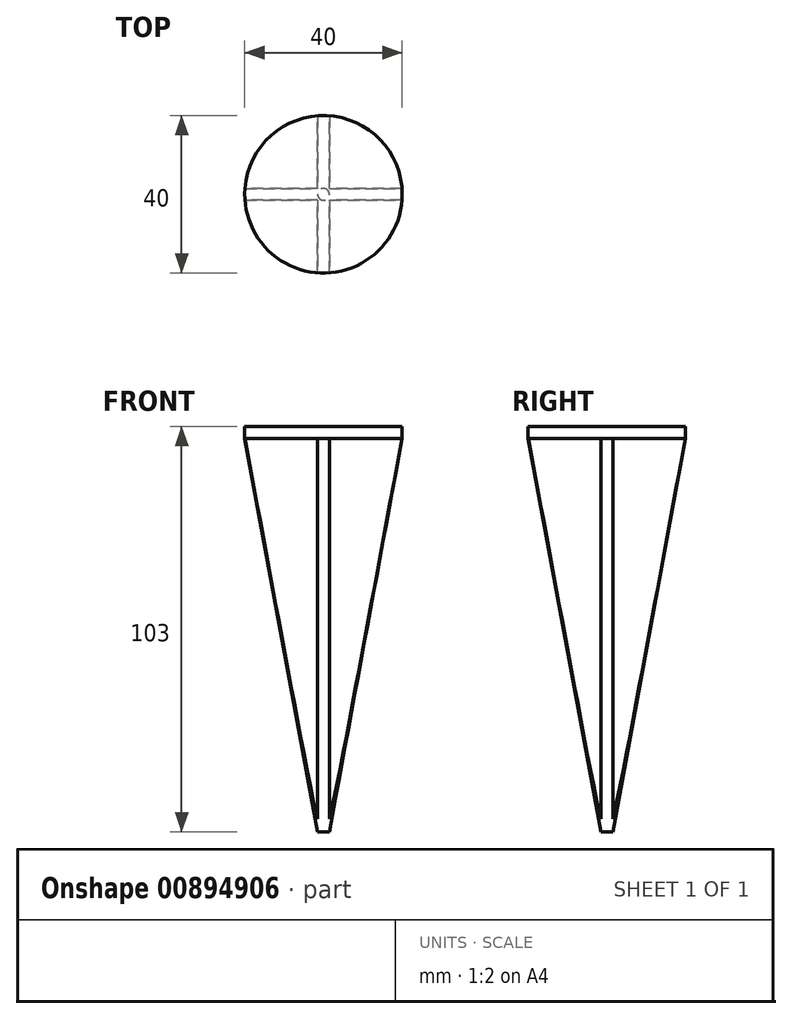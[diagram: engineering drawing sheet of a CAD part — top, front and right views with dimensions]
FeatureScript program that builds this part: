
annotation { "Feature Type Name" : "Feature", "Feature Type Description" : "" }
export const myFeature = defineFeature(function(context is Context, id is Id, definition is map)
    precondition{}
    {
        {
            var Q0;
            Q0=qCreatedBy(makeId("Top.planeOp"),FACE);
            var sketch = newSketch(context, id + "F0", { "sketchPlane" : qUnion([Q0])});
            skCircle(sketch, "E0", {"center": v(0, 0) * mm, "radius": 20 * mm});
            skLineSegment(sketch, "E1.bottom", {"start": v(-19.94, -1.5) * mm, "end": v(-1.5, -1.5) * mm});
            skLineSegment(sketch, "E1.top", {"start": v(-19.94, 1.5) * mm, "end": v(-1.5, 1.5) * mm});
            skLineSegment(sketch, "E2.left", {"start": v(1.5, -19.94) * mm, "end": v(1.5, -1.5) * mm});
            skLineSegment(sketch, "E2.right", {"start": v(-1.5, -19.94) * mm, "end": v(-1.5, -1.5) * mm});
            skLineSegment(sketch, "E3.trimOffspring", {"start": v(-1.5, 1.5) * mm, "end": v(-1.5, 19.94) * mm});
            skLineSegment(sketch, "E4.trimOffspring", {"start": v(1.5, 1.5) * mm, "end": v(19.94, 1.5) * mm});
            skLineSegment(sketch, "E5.trimOffspring", {"start": v(1.5, 1.5) * mm, "end": v(1.5, 19.94) * mm});
            skLineSegment(sketch, "E6.trimOffspring", {"start": v(1.5, -1.5) * mm, "end": v(19.94, -1.5) * mm});
            skSolve(sketch);
        }
        {
            var Q0;
            {var subQ0=sQuery(id+"F0.wireOp",EDGE,"E1.top");Q0=makeQuery(id+"F0.imprint","IMPRINT",FACE,{"disambiguationData":[TD([[makeQuery(id+"F0.imprint","IMPRINT",EDGE,{"derivedFrom":subQ0}),1.0]])]});}
            var Q1;
            {var subQ4=sQuery(id+"F0.wireOp",EDGE,"E1.bottom");Q1=makeQuery(id+"F0.imprint","IMPRINT",FACE,{"disambiguationData":[TD([[makeQuery(id+"F0.imprint","IMPRINT",EDGE,{"derivedFrom":subQ4}),1.0]])]});}
            var Q2;
            {var subQ0=sQuery(id+"F0.wireOp",EDGE,"E4.trimOffspring");Q2=makeQuery(id+"F0.imprint","IMPRINT",FACE,{"disambiguationData":[TD([[makeQuery(id+"F0.imprint","IMPRINT",EDGE,{"derivedFrom":subQ0}),1.0]])]});}
            var Q3;
            {var subQ0=sQuery(id+"F0.wireOp",EDGE,"E2.left");Q3=makeQuery(id+"F0.imprint","IMPRINT",FACE,{"disambiguationData":[TD([[makeQuery(id+"F0.imprint","IMPRINT",EDGE,{"derivedFrom":subQ0}),-1.0]])]});}
            var Q4;
            {var subQ0=sQuery(id+"F0.wireOp",EDGE,"E1.bottom");Q4=makeQuery(id+"F0.imprint","IMPRINT",FACE,{"disambiguationData":[TD([[makeQuery(id+"F0.imprint","IMPRINT",EDGE,{"derivedFrom":subQ0}),-1.0]])]});}
            extrude(context, id + "F1", {"entities" : qUnion([Q0, Q1, Q2, Q3, Q4]), "depth" : 3 * mm, "offsetDistance" : 25 * mm});
        }
        {
            var Q0;
            {var subQ4=sQuery(id+"F0.wireOp",EDGE,"E1.bottom");Q0=makeQuery(id+"F0.imprint","IMPRINT",FACE,{"disambiguationData":[TD([[makeQuery(id+"F0.imprint","IMPRINT",EDGE,{"derivedFrom":subQ4}),1.0]])]});}
            extrude(context, id + "F2", {"entities" : qUnion([Q0]), "operationType" : NewBodyOperationType.ADD, "oppositeDirection" : true, "depth" : 100 * mm, "offsetDistance" : 25 * mm});
        }
        {
            var Q0;
            Q0=qCreatedBy(makeId("Front.planeOp"),FACE);
            var sketch = newSketch(context, id + "F3", { "sketchPlane" : qUnion([Q0])});
            skLineSegment(sketch, "E7", {"start": v(-1.5, -100) * mm, "end": v(-20, 0) * mm});
            skLineSegment(sketch, "E8", {"start": v(-20, 0) * mm, "end": v(-20, -100) * mm});
            skLineSegment(sketch, "E9", {"start": v(-20, -100) * mm, "end": v(-1.5, -100) * mm});
            skLineSegment(sketch, "E10", {"start": v(0, 0) * mm, "end": v(0, -111.98) * mm, "construction": true});
            skSolve(sketch);
        }
        {
            var Q0;
            Q0=makeQuery(id+"F3.imprint","IMPRINT",FACE,{"disambiguationData":[TD([[makeQuery(id+"F3.imprint","IMPRINT",EDGE,{"derivedFrom":sQuery(id+"F3.wireOp",EDGE,"E7")}),1.0]])]});
            var Q1;
            Q1=sQuery(id+"F3.wireOp",EDGE,"E10");
            revolve(context, id + "F4", {"operationType" : NewBodyOperationType.REMOVE, "surfaceOperationType" : NewSurfaceOperationType.NEW, "entities" : qUnion([Q0]), "axis" : qUnion([Q1]), "revolveType" : RevolveType.FULL});
        }
    });
